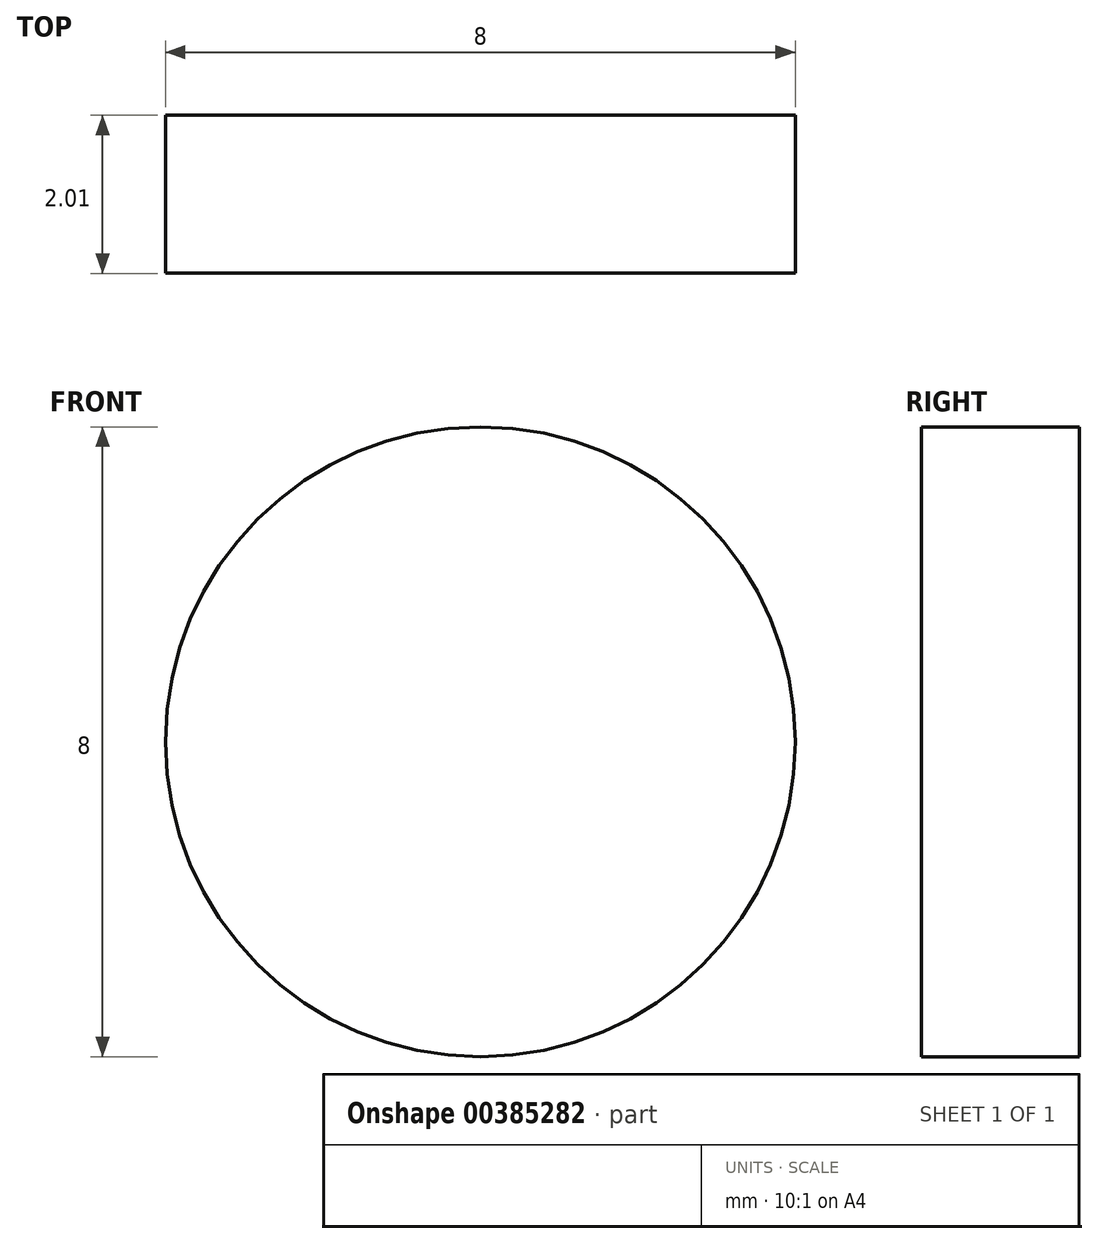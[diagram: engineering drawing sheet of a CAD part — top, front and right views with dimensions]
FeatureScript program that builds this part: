
annotation { "Feature Type Name" : "Feature", "Feature Type Description" : "" }
export const myFeature = defineFeature(function(context is Context, id is Id, definition is map)
    precondition{}
    {
        {
            var Q0;
            Q0=qCreatedBy(makeId("Front.planeOp"),FACE);
            var sketch = newSketch(context, id + "F0", { "sketchPlane" : qUnion([Q0])});
            skCircle(sketch, "E0", {"center": v(0, 0) * mm, "radius": 3 * mm});
            skCircle(sketch, "E1", {"center": v(0, 0) * mm, "radius": 4 * mm});
            skSolve(sketch);
        }
        {
            var Q0;
            Q0=makeQuery(id+"F0.imprint","IMPRINT",FACE,{"disambiguationData":[TD([[makeQuery(id+"F0.imprint","IMPRINT",EDGE,{"derivedFrom":sQuery(id+"F0.wireOp",EDGE,"E0")}),-1.0]])]});
            var Q1;
            Q1=makeQuery(id+"F0.imprint","IMPRINT",FACE,{"disambiguationData":[TD([[makeQuery(id+"F0.imprint","IMPRINT",EDGE,{"derivedFrom":sQuery(id+"F0.wireOp",EDGE,"E0")}),1.0]])]});
            extrude(context, id + "F1", {"entities" : qUnion([Q0, Q1]), "depth" : 2 * mm});
        }
    });
